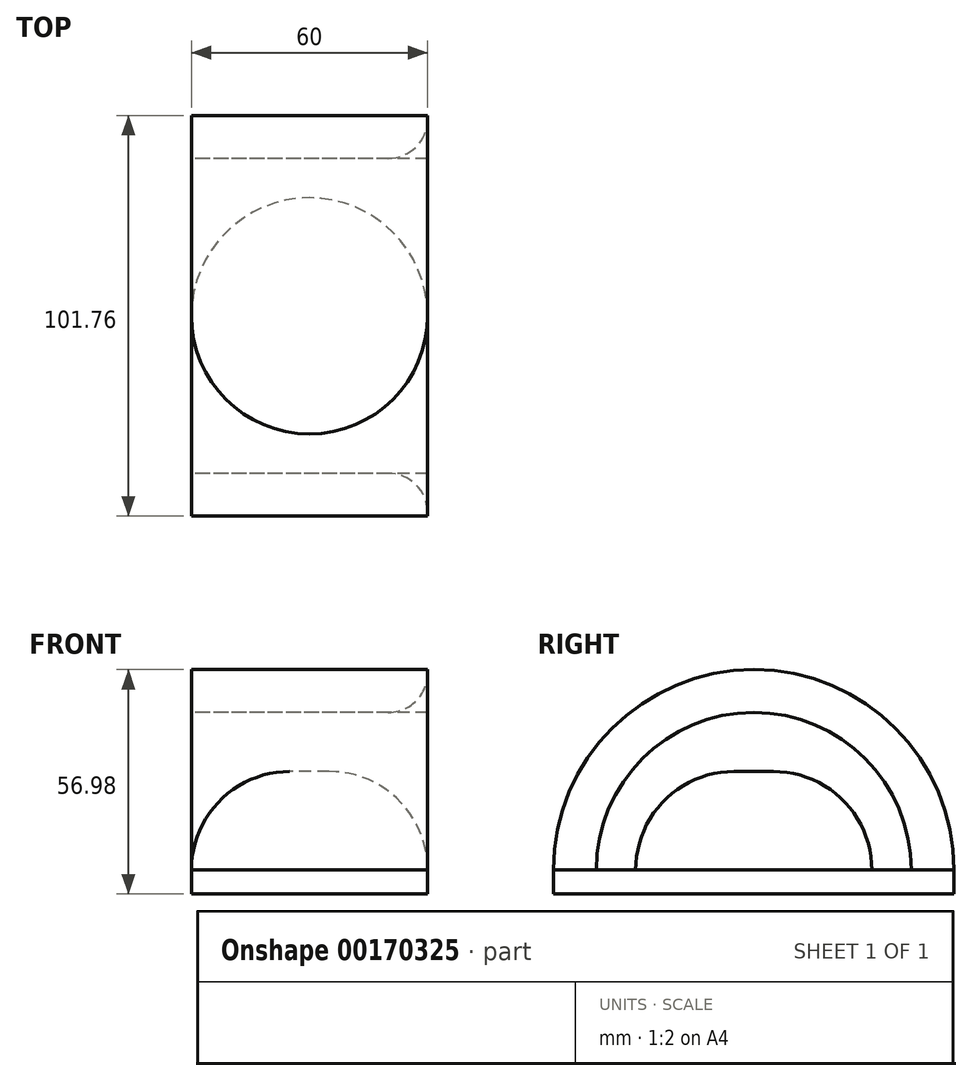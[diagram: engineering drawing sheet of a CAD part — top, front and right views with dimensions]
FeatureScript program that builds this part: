
annotation { "Feature Type Name" : "Feature", "Feature Type Description" : "" }
export const myFeature = defineFeature(function(context is Context, id is Id, definition is map)
    precondition{}
    {
        {
            var Q0;
            Q0=qCreatedBy(makeId("Top.planeOp"),FACE);
            var sketch = newSketch(context, id + "F0", { "sketchPlane" : qUnion([Q0])});
            skCircle(sketch, "E0", {"center": v(0, 0) * mm, "radius": 30 * mm});
            skSolve(sketch);
        }
        {
            var Q0;
            Q0=makeQuery(id+"F0.imprint","IMPRINT",FACE,{"disambiguationData":[TD([[makeQuery(id+"F0.imprint","IMPRINT",EDGE,{"derivedFrom":sQuery(id+"F0.wireOp",EDGE,"E0")}),1.0]])]});
            extrude(context, id + "F1", {"entities" : qUnion([Q0]), "depth" : 25 * mm});
        }
        {
            var Q0;
            Q0=makeQuery(id+"F1.opExtrude","CAP_EDGE",EDGE,{"disambiguationData":[OSD([sQuery(id+"F0.wireOp",EDGE,"E0")])],"isStart":false});
            fillet(context, id + "F2", {"entities" : qUnion([Q0]), "radius" : 25 * mm, "tangentPropagation" : true, "allowEdgeOverflow" : false});
        }
        {
            var Q0;
            Q0=qCreatedBy(makeId("Right.planeOp"),FACE);
            var sketch = newSketch(context, id + "F3", { "sketchPlane" : qUnion([Q0])});
            skLineSegment(sketch, "E1", {"start": v(-50.88, 0) * mm, "end": v(50.88, 0) * mm});
            skArc(sketch, "E2", {"start": v(40, 0) * mm, "mid": v(0, 40) * mm, "end": v(-40, 0) * mm});
            skArc(sketch, "E3", {"start": v(50.88, 0) * mm, "mid": v(0, 50.88) * mm, "end": v(-50.88, 0) * mm});
            skLineSegment(sketch, "E4", {"start": v(-50.88, 0) * mm, "end": v(-50.88, -6.1) * mm});
            skLineSegment(sketch, "E5", {"start": v(-50.88, -6.1) * mm, "end": v(50.88, -6.1) * mm});
            skLineSegment(sketch, "E6", {"start": v(50.88, -6.1) * mm, "end": v(50.88, 0) * mm});
            skSolve(sketch);
        }
        {
            var Q0;
            {var subQ2=sQuery(id+"F3.wireOp",EDGE,"E2");Q0=makeQuery(id+"F3.imprint","IMPRINT",FACE,{"disambiguationData":[TD([[makeQuery(id+"F3.imprint","IMPRINT",EDGE,{"derivedFrom":subQ2}),-1.0]])]});}
            extrude(context, id + "F4", {"entities" : qUnion([Q0]), "depth" : 30 * mm, "hasSecondDirection" : true, "secondDirectionOppositeDirection" : true, "secondDirectionDepth" : 30 * mm});
        }
        {
            var Q0;
            Q0 = qSketchRegion(id + "F3", true);
            extrude(context, id + "F5", {"entities" : qUnion([Q0]), "depth" : 30 * mm, "hasSecondDirection" : true, "secondDirectionOppositeDirection" : true, "secondDirectionDepth" : 30 * mm});
        }
        {
            var Q0;
            Q0=makeQuery(id+"F5.opExtrude","CAP_EDGE",EDGE,{"disambiguationData":[OSD([sQuery(id+"F3.wireOp",EDGE,"E2")])],"isStart":false});
            fillet(context, id + "F6", {"entities" : qUnion([Q0]), "radius" : 10 * mm, "tangentPropagation" : true, "allowEdgeOverflow" : false});
        }
    });
